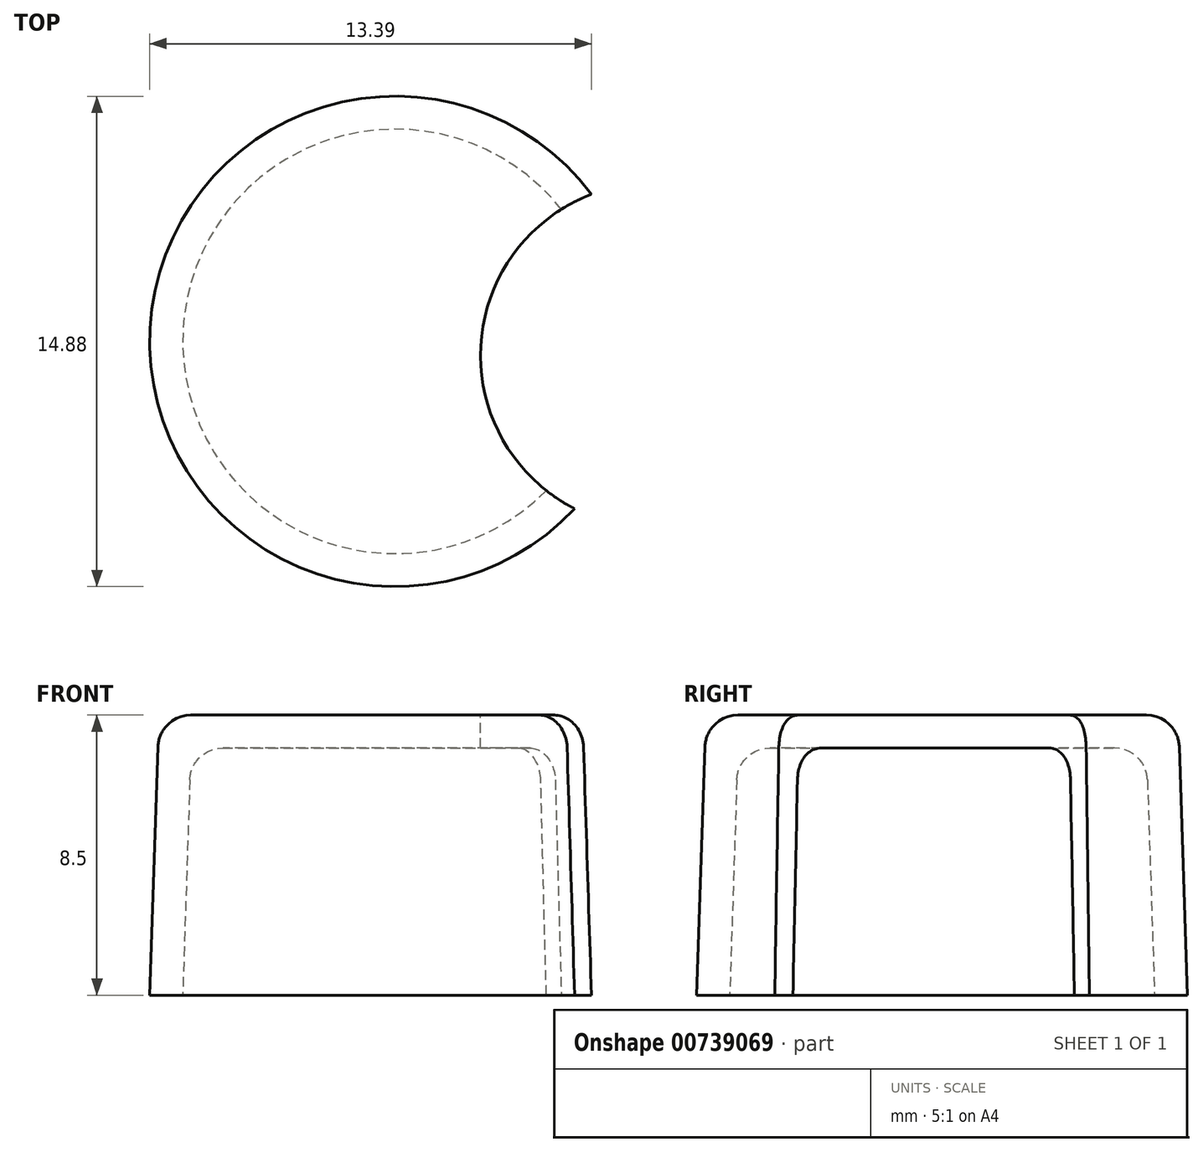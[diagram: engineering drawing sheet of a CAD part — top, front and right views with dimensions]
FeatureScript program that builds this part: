
annotation { "Feature Type Name" : "Feature", "Feature Type Description" : "" }
export const myFeature = defineFeature(function(context is Context, id is Id, definition is map)
    precondition{}
    {
        {
            var Q0;
            Q0=qCreatedBy(makeId("Front.planeOp"),FACE);
            var sketch = newSketch(context, id + "F0", { "sketchPlane" : qUnion([Q0])});
            skLineSegment(sketch, "E0", {"start": v(-4.7, 6.53) * mm, "end": v(-4.9, 0) * mm});
            skPoint(sketch, "E1.visualSharp", {"position": v(-4.66, 7.5) * mm});
            skArc(sketch, "E1.filletArc", {"start": v(-3.7, 7.5) * mm, "mid": v(-4.4, 7.22) * mm, "end": v(-4.7, 6.53) * mm});
            skLineSegment(sketch, "E2", {"start": v(-5.91, 0) * mm, "end": v(-5.66, 7.53) * mm});
            skLineSegment(sketch, "E3", {"start": v(-4.9, 0) * mm, "end": v(-5.91, 0) * mm});
            skArc(sketch, "E4.filletArc", {"start": v(-4.66, 8.5) * mm, "mid": v(-5.36, 8.22) * mm, "end": v(-5.66, 7.53) * mm});
            skPoint(sketch, "E5", {"position": v(1.53, 7.5) * mm});
            skLineSegment(sketch, "E6", {"start": v(1.53, 10.76) * mm, "end": v(1.53, -2.27) * mm, "construction": true});
            skLineSegment(sketch, "E7", {"start": v(-4.66, 8.5) * mm, "end": v(1.53, 8.5) * mm});
            skLineSegment(sketch, "E8", {"start": v(-3.7, 7.5) * mm, "end": v(1.53, 7.5) * mm});
            skLineSegment(sketch, "E9", {"start": v(-4.9, 0) * mm, "end": v(1.53, 0) * mm});
            skLineSegment(sketch, "E10", {"start": v(1.53, 0) * mm, "end": v(1.53, 8.5) * mm});
            skSolve(sketch);
        }
        {
            var Q0;
            Q0=makeQuery(id+"F0.imprint","IMPRINT",FACE,{"disambiguationData":[TD([[makeQuery(id+"F0.imprint","IMPRINT",EDGE,{"derivedFrom":sQuery(id+"F0.wireOp",EDGE,"E0")}),-1.0]])]});
            var Q1;
            Q1=sQuery(id+"F0.wireOp",EDGE,"E10");
            revolve(context, id + "F1", {"surfaceOperationType" : NewSurfaceOperationType.NEW, "entities" : qUnion([Q0]), "axis" : qUnion([Q1]), "revolveType" : RevolveType.FULL});
        }
        {
            var Q0;
            Q0=makeQuery(id+"F1.opRevolve","SWEPT_FACE",FACE,{"disambiguationData":[OSD([sQuery(id+"F0.wireOp",EDGE,"E7")])]});
            var sketch = newSketch(context, id + "F2", { "sketchPlane" : qUnion([Q0])});
            skArc(sketch, "E11", {"start": v(8.45, 4.73) * mm, "mid": v(4.31, -1.82) * mm, "end": v(11.24, -5.3) * mm});
            skLineSegment(sketch, "E12", {"start": v(8.45, 4.73) * mm, "end": v(11.24, -5.3) * mm});
            skSolve(sketch);
        }
        {
            var Q0;
            {var subQ0=sQuery(id+"F2.wireOp",EDGE,"E11");var subQ1=makeQuery(id+"F1.opRevolve","SWEPT_EDGE",EDGE,{"disambiguationData":[OSD([sQuery(id+"F0.wireOp",EDGE,"E4.filletArc"),sQuery(id+"F0.wireOp",EDGE,"E7")])]});var subQ2=makeQuery(id+"F2.imprint","INTERSECT",VERTEX,{"disambiguationData":[OD(0.0)],"derivedFrom":[subQ1,subQ0]});Q0=makeQuery(id+"F2.imprint","IMPRINT",FACE,{"disambiguationData":[TD([[makeQuery(id+"F2.imprint","IMPRINT",EDGE,{"disambiguationData":[TD([[subQ2,-1.0]])],"derivedFrom":subQ0}),1.0]])]});}
            var Q1;
            {var subQ0=sQuery(id+"F2.wireOp",EDGE,"E12");Q1=makeQuery(id+"F2.imprint","IMPRINT",FACE,{"disambiguationData":[TD([[makeQuery(id+"F2.imprint","IMPRINT",EDGE,{"derivedFrom":subQ0}),-1.0]])]});}
            extrude(context, id + "F3", {"entities" : qUnion([Q0, Q1]), "operationType" : NewBodyOperationType.REMOVE, "oppositeDirection" : true, "depth" : 12 * mm, "offsetDistance" : 25 * mm});
        }
    });
